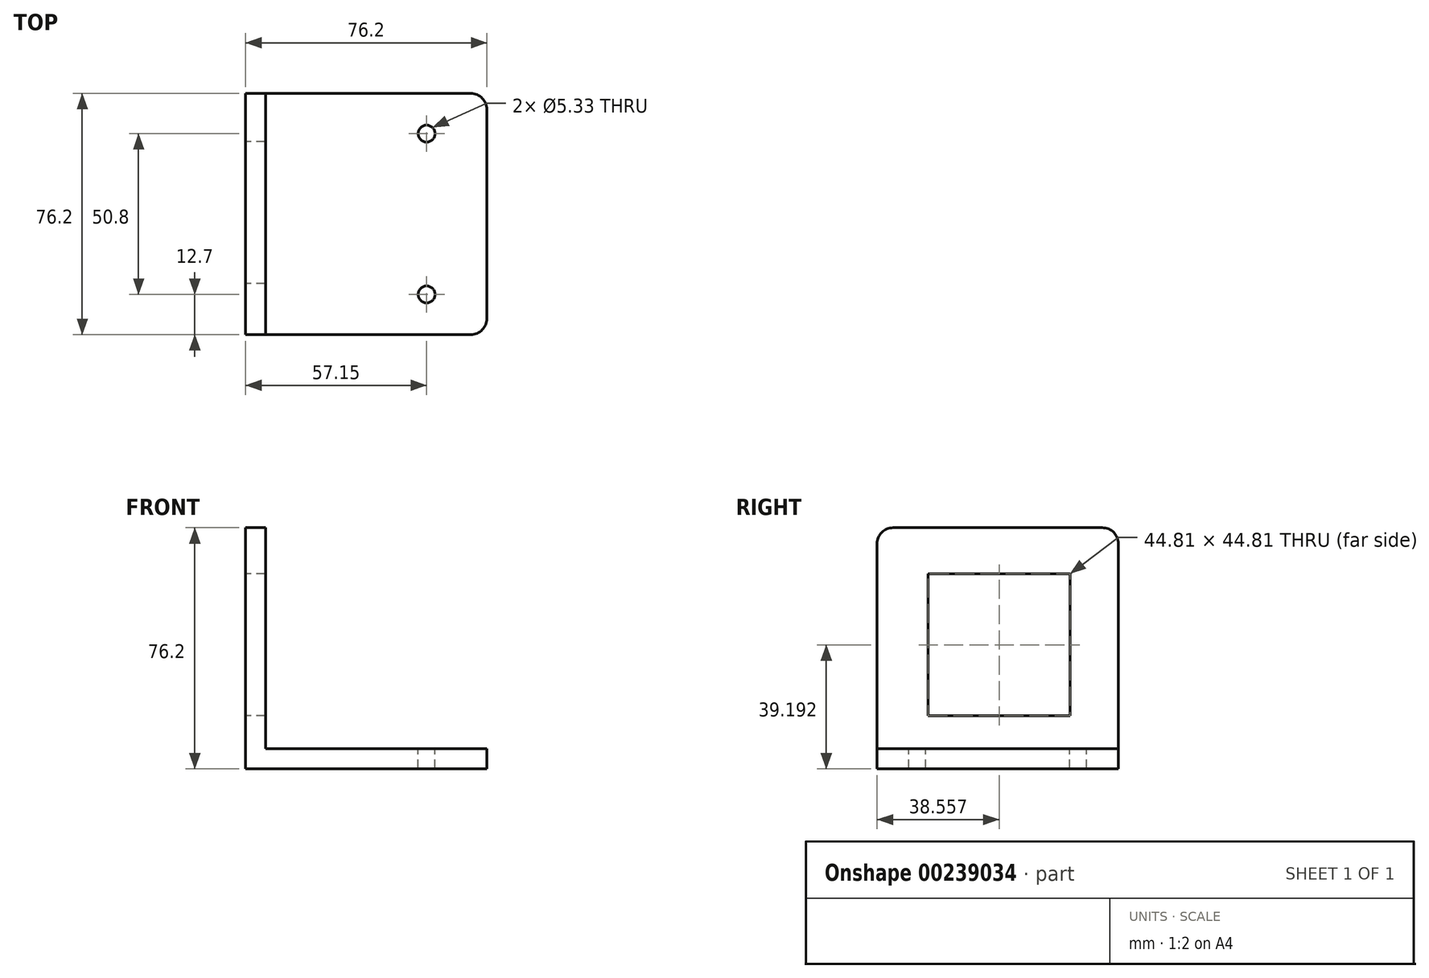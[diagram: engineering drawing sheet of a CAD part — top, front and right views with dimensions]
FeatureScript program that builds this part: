
annotation { "Feature Type Name" : "Feature", "Feature Type Description" : "" }
export const myFeature = defineFeature(function(context is Context, id is Id, definition is map)
    precondition{}
    {
        {
            var Q0;
            Q0=qCreatedBy(makeId("Front.planeOp"),FACE);
            var sketch = newSketch(context, id + "F0", { "sketchPlane" : qUnion([Q0])});
            skLineSegment(sketch, "E0", {"start": v(0, 0) * mm, "end": v(0, 76.2) * mm});
            skLineSegment(sketch, "E1", {"start": v(0, 76.2) * mm, "end": v(6.35, 76.2) * mm});
            skLineSegment(sketch, "E2", {"start": v(6.35, 76.2) * mm, "end": v(6.35, 6.35) * mm});
            skLineSegment(sketch, "E3", {"start": v(6.35, 6.35) * mm, "end": v(76.2, 6.35) * mm});
            skLineSegment(sketch, "E4", {"start": v(76.2, 6.35) * mm, "end": v(76.2, 0) * mm});
            skLineSegment(sketch, "E5", {"start": v(76.2, 0) * mm, "end": v(0, 0) * mm});
            skSolve(sketch);
        }
        {
            var Q0;
            Q0=makeQuery(id+"F0.imprint","IMPRINT",FACE,{"disambiguationData":[TD([[makeQuery(id+"F0.imprint","IMPRINT",EDGE,{"derivedFrom":sQuery(id+"F0.wireOp",EDGE,"E0")}),-1.0]])]});
            extrude(context, id + "F1", {"entities" : qUnion([Q0]), "depth" : 76.2 * mm});
        }
        {
            var Q0;
            Q0=makeQuery(id+"F1.opExtrude","SWEPT_FACE",FACE,{"disambiguationData":[OSD([sQuery(id+"F0.wireOp",EDGE,"E0")])]});
            var sketch = newSketch(context, id + "F2", { "sketchPlane" : qUnion([Q0])});
            skLineSegment(sketch, "E6.bottom", {"start": v(15.24, 16.79) * mm, "end": v(60.05, 16.79) * mm});
            skLineSegment(sketch, "E6.top", {"start": v(15.24, 61.6) * mm, "end": v(60.05, 61.6) * mm});
            skLineSegment(sketch, "E6.left", {"start": v(15.24, 16.79) * mm, "end": v(15.24, 61.6) * mm});
            skLineSegment(sketch, "E6.right", {"start": v(60.05, 16.79) * mm, "end": v(60.05, 61.6) * mm});
            skSolve(sketch);
        }
        {
            var Q0;
            Q0=makeQuery(id+"F2.imprint","IMPRINT",FACE,{"disambiguationData":[TD([[makeQuery(id+"F2.imprint","IMPRINT",EDGE,{"derivedFrom":sQuery(id+"F2.wireOp",EDGE,"E6.bottom")}),1.0]])]});
            extrude(context, id + "F3", {"entities" : qUnion([Q0]), "operationType" : NewBodyOperationType.REMOVE, "oppositeDirection" : true, "depth" : 25.4 * mm});
        }
        {
            var Q0;
            Q0=makeQuery(id+"F1.opExtrude","SWEPT_FACE",FACE,{"disambiguationData":[OSD([sQuery(id+"F0.wireOp",EDGE,"E3")])]});
            var sketch = newSketch(context, id + "F4", { "sketchPlane" : qUnion([Q0])});
            skPoint(sketch, "E7", {"position": v(57.15, -12.7) * mm});
            skPoint(sketch, "E8", {"position": v(57.15, -63.5) * mm});
            skSolve(sketch);
        }
        {
            var Q0;
            Q0=sQuery(id+"F4.wireOp",VERTEX,"E7");
            var Q1;
            Q1=sQuery(id+"F4.wireOp",VERTEX,"E8");
            var Q2;
            Q2=makeQuery(id+"F1.opExtrude","SWEPT_BODY",BODY,{"disambiguationData":[OSD([sQuery(id+"F0.wireOp",EDGE,"E0"),sQuery(id+"F0.wireOp",EDGE,"E1"),sQuery(id+"F0.wireOp",EDGE,"E2"),sQuery(id+"F0.wireOp",EDGE,"E3"),sQuery(id+"F0.wireOp",EDGE,"E4"),sQuery(id+"F0.wireOp",EDGE,"E5")])]});
            hole(context, id + "F5", {"style" : HoleStyle.SIMPLE, "endStyle" : HoleEndStyle.BLIND, "holeDiameter" : 5.33 * mm, "holeDepth" : 12.7 * mm, "locations" : qUnion([Q0, Q1]), "scope" : qUnion([Q2])});
        }
        {
            var Q0;
            Q0=makeQuery(id+"F1.opExtrude","CAP_EDGE",EDGE,{"disambiguationData":[OSD([sQuery(id+"F0.wireOp",EDGE,"E1")])],"isStart":true});
            var Q1;
            Q1=makeQuery(id+"F1.opExtrude","CAP_EDGE",EDGE,{"disambiguationData":[OSD([sQuery(id+"F0.wireOp",EDGE,"E1")])],"isStart":false});
            var Q2;
            Q2=makeQuery(id+"F1.opExtrude","CAP_EDGE",EDGE,{"disambiguationData":[OSD([sQuery(id+"F0.wireOp",EDGE,"E4")])],"isStart":false});
            var Q3;
            Q3=makeQuery(id+"F1.opExtrude","CAP_EDGE",EDGE,{"disambiguationData":[OSD([sQuery(id+"F0.wireOp",EDGE,"E4")])],"isStart":true});
            fillet(context, id + "F6", {"entities" : qUnion([Q0, Q1, Q2, Q3]), "radius" : 5.08 * mm, "tangentPropagation" : true, "allowEdgeOverflow" : false});
        }
    });
